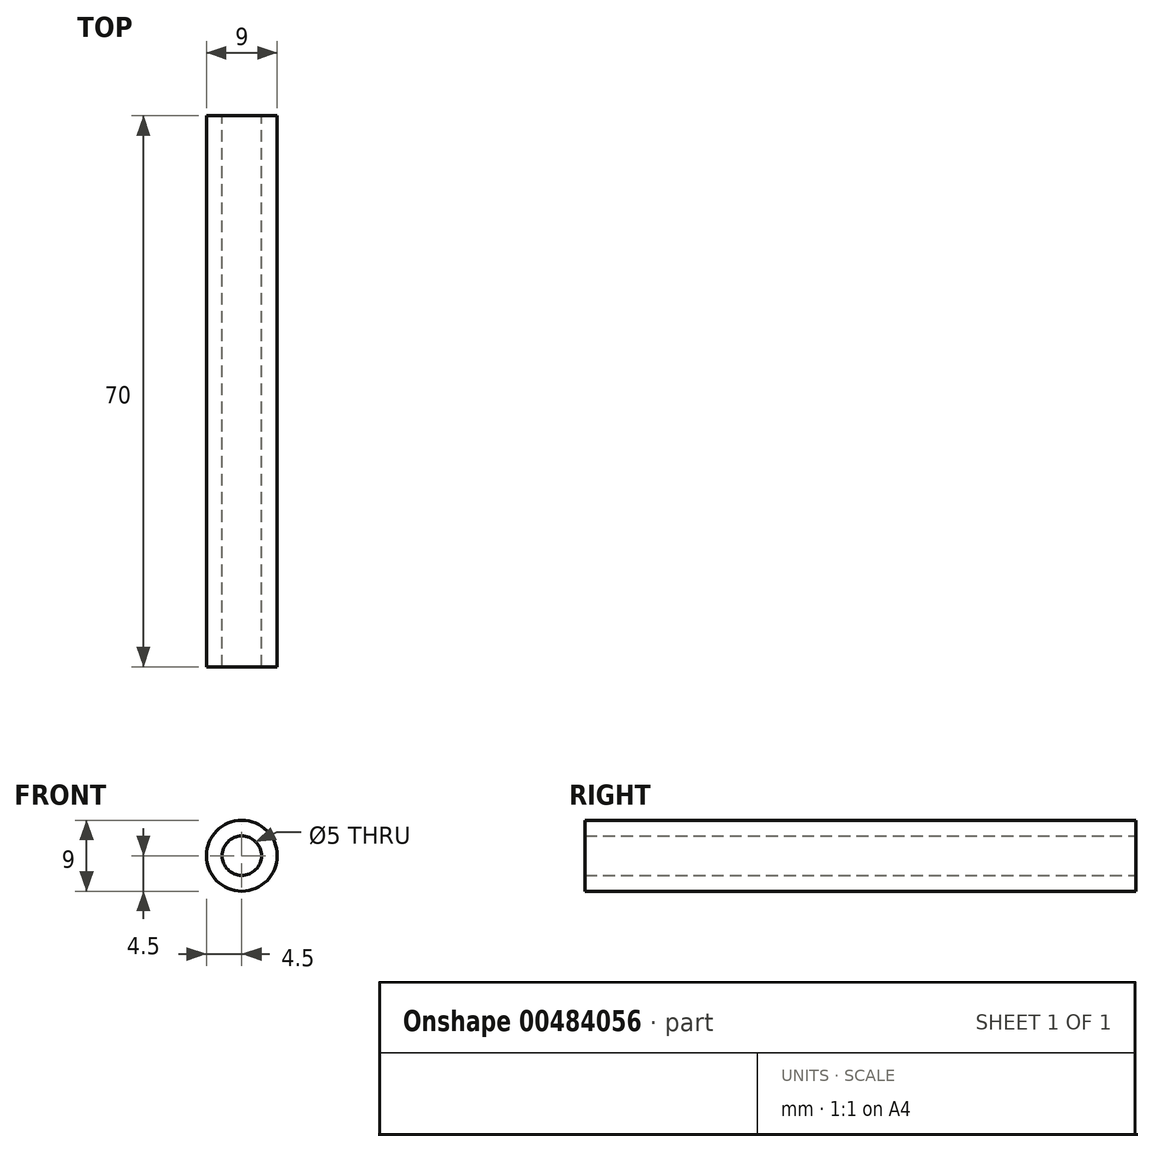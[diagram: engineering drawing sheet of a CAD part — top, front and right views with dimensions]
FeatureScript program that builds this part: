
annotation { "Feature Type Name" : "Feature", "Feature Type Description" : "" }
export const myFeature = defineFeature(function(context is Context, id is Id, definition is map)
    precondition{}
    {
        {
            var Q0;
            Q0=qCreatedBy(makeId("Front.planeOp"),FACE);
            var sketch = newSketch(context, id + "F0", { "sketchPlane" : qUnion([Q0])});
            skCircle(sketch, "E0", {"center": v(0, 0) * mm, "radius": 4.5 * mm});
            skCircle(sketch, "E1", {"center": v(0, 0) * mm, "radius": 2.5 * mm});
            skSolve(sketch);
        }
        {
            var Q0;
            Q0 = qSketchRegion(id + "F0", true);
            extrude(context, id + "F1", {"entities" : qUnion([Q0]), "endBound" : BoundingType.SYMMETRIC, "depth" : 70 * mm});
        }
    });
